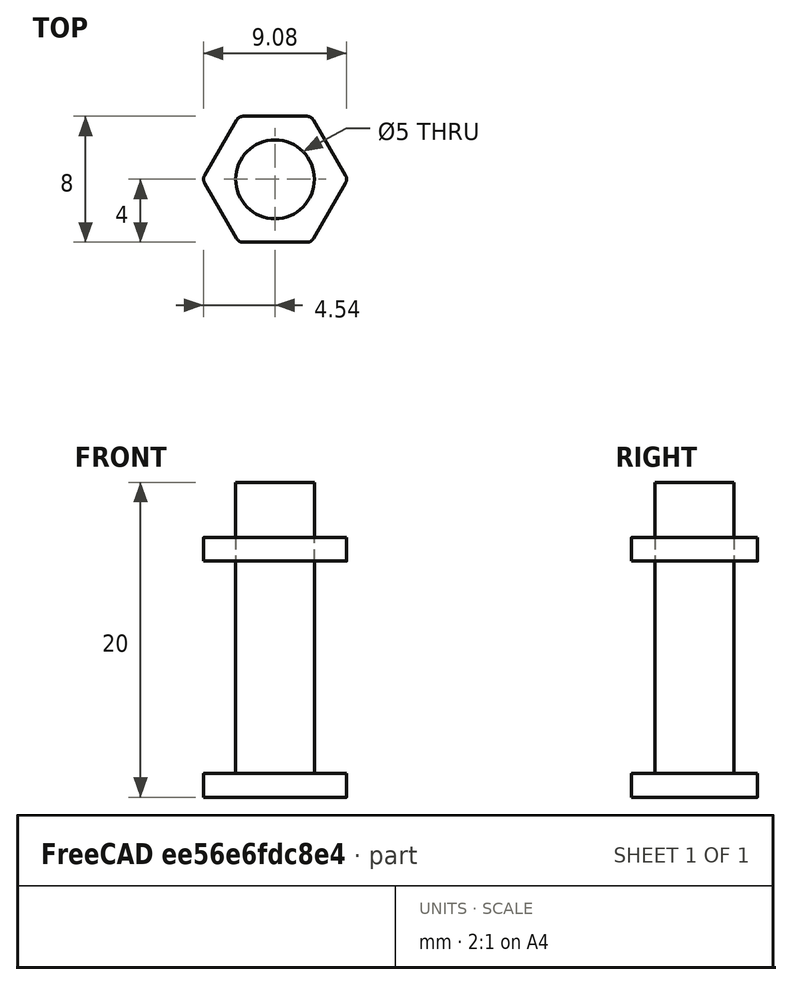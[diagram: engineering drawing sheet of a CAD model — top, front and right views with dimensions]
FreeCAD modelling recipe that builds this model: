
FCSTD DOCUMENT  (FreeCAD 0.14R2935 (Git))
Label: vis_ecrou
License: CC-BY 3.0
LicenseURL: http://creativecommons.org/licenses/by/3.0/
objects: Part::Part2DObjectPython×4, Part::Extrusion×4, Part::Cut×1, Part::MultiFuse×1
note: 10 computed .brp shape members not serialized (recipe doc carries the construction recipe); baked Part::Feature solids carry a one-line shape summary decoded from their .brp

FEATURE [Part::Part2DObjectPython] Polygon  # Draft 2D object (typed FeaturePython)
  ChamferSize = 0
  DrawMode = 1
  FacesNumber = 6
  FilletRadius = 0.5
  Radius = 4
FEATURE [Part::Part2DObjectPython] Circle  # Draft 2D object (typed FeaturePython)
  FirstAngle = 0
  LastAngle = 0
  Placement = pos=(0,0,0) rot=(1,0,0;3.14159rad)
  Radius = 2.5
  Support = -> Polygon
FEATURE [Part::Part2DObjectPython] Polygon001  # Draft 2D object (typed FeaturePython)
  ChamferSize = 0
  DrawMode = 1
  FacesNumber = 6
  FilletRadius = 0.5
  Placement = pos=(10,0,0) rot=(0,0,1;0rad)
  Radius = 4
FEATURE [Part::Part2DObjectPython] Circle001  # Draft 2D object (typed FeaturePython)
  FirstAngle = 0
  LastAngle = 0
  Placement = pos=(10,0,0) rot=(1,0,0;3.14159rad)
  Radius = 2.5
  Support = -> Polygon001
FEATURE [Part::Extrusion] Extrude
  Base = -> Circle
  Dir = (0,0,20)
  Solid = true
FEATURE [Part::Extrusion] Extrude001
  Base = -> Polygon
  Dir = (0,0,1.5)
  Solid = false
FEATURE [Part::Extrusion] Extrude002
  Base = -> Circle001
  Dir = (0,0,1.5)
  Solid = false
FEATURE [Part::Extrusion] Extrude003
  Base = -> Polygon001
  Dir = (0,0,1.5)
  Solid = false
FEATURE [Part::Cut] Cut  label="ecrou"
  Base = -> Extrude003
  Placement = pos=(-10,0,15) rot=(0,0,1;0rad)
  Tool = -> Extrude002
FEATURE [Part::MultiFuse] Fusion  label="vis"
  Shapes = -> [Extrude,Extrude001]
